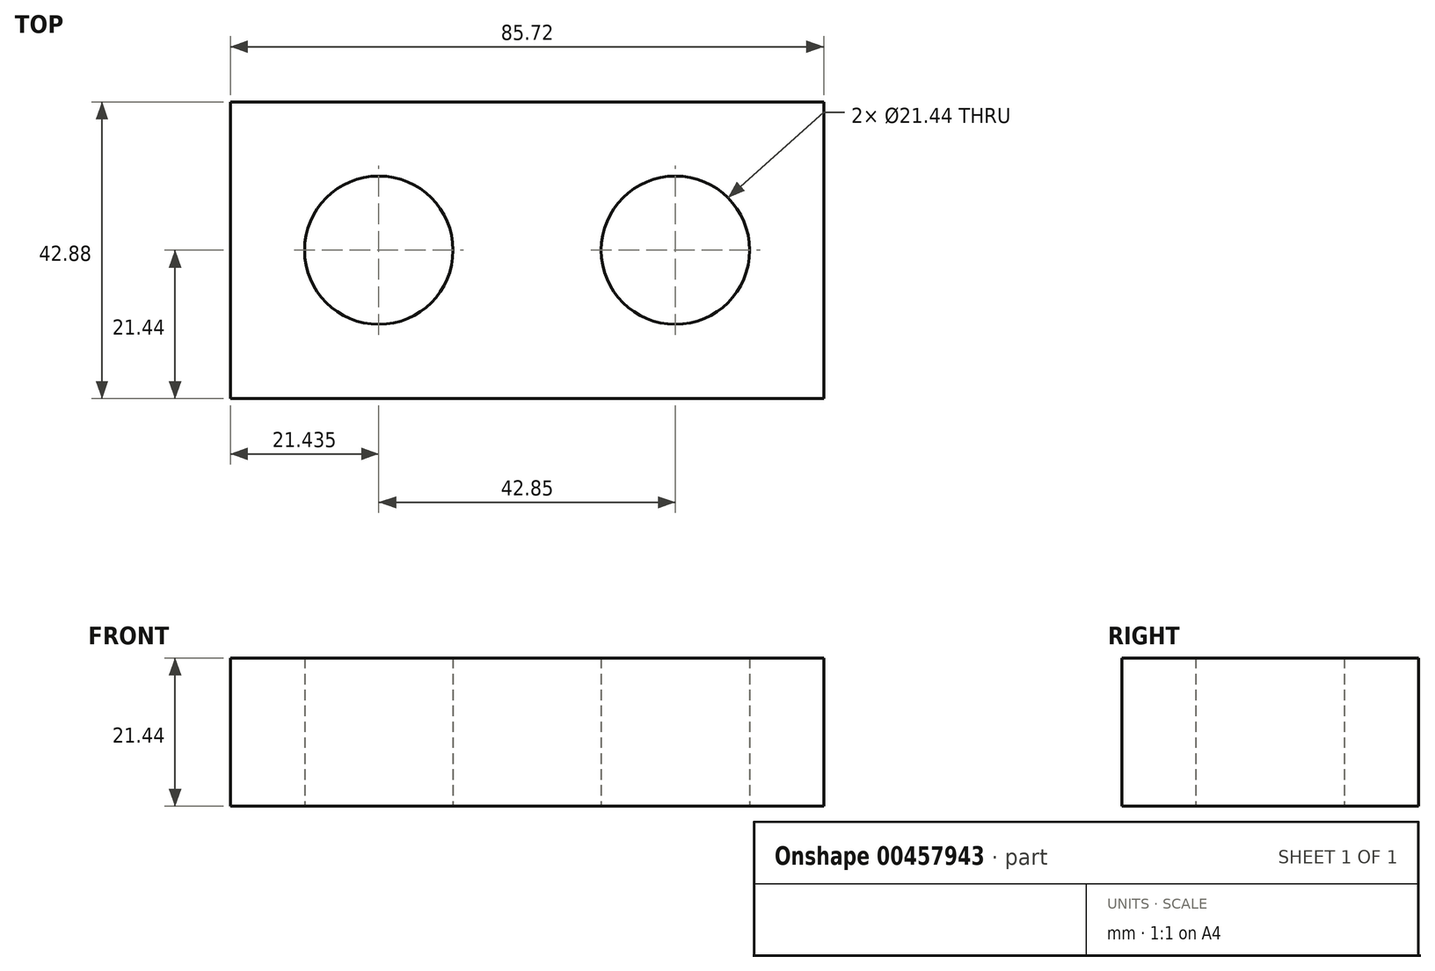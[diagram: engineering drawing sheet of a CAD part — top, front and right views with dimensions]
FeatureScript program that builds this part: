
annotation { "Feature Type Name" : "Feature", "Feature Type Description" : "" }
export const myFeature = defineFeature(function(context is Context, id is Id, definition is map)
    precondition{}
    {
        {
            var Q0;
            Q0=qCreatedBy(makeId("Top.planeOp"),FACE);
            var sketch = newSketch(context, id + "F0", { "sketchPlane" : qUnion([Q0])});
            skLineSegment(sketch, "E0.bottom", {"start": v(42.86, 21.44) * mm, "end": v(-42.86, 21.44) * mm});
            skLineSegment(sketch, "E0.top", {"start": v(42.86, -21.44) * mm, "end": v(-42.86, -21.44) * mm});
            skLineSegment(sketch, "E0.left", {"start": v(42.86, 21.44) * mm, "end": v(42.86, -21.44) * mm});
            skLineSegment(sketch, "E0.right", {"start": v(-42.86, 21.44) * mm, "end": v(-42.86, -21.44) * mm});
            skPoint(sketch, "E0.middle", {"position": v(0, 0) * mm});
            skPoint(sketch, "E1.orphan", {"position": v(-42.86, 0) * mm});
            skPoint(sketch, "E2.orphan", {"position": v(0, 21.44) * mm});
            skPoint(sketch, "E3.end.orphan", {"position": v(0, -21.44) * mm});
            skPoint(sketch, "E4.end.orphan", {"position": v(42.86, 0) * mm});
            skLineSegment(sketch, "E5", {"start": v(0, 21.44) * mm, "end": v(0, -21.44) * mm, "construction": true});
            skCircle(sketch, "E6", {"center": v(-21.42, 0) * mm, "radius": 10.72 * mm});
            skCircle(sketch, "E7", {"center": v(21.42, 0) * mm, "radius": 10.72 * mm});
            skSolve(sketch);
        }
        {
            var Q0;
            Q0=makeQuery(id+"F0.imprint","IMPRINT",FACE,{"disambiguationData":[TD([[makeQuery(id+"F0.imprint","IMPRINT",EDGE,{"derivedFrom":sQuery(id+"F0.wireOp",EDGE,"E0.bottom")}),1.0]])]});
            extrude(context, id + "F1", {"entities" : qUnion([Q0]), "depth" : 21.44 * mm, "offsetDistance" : 25.4 * mm});
        }
    });
